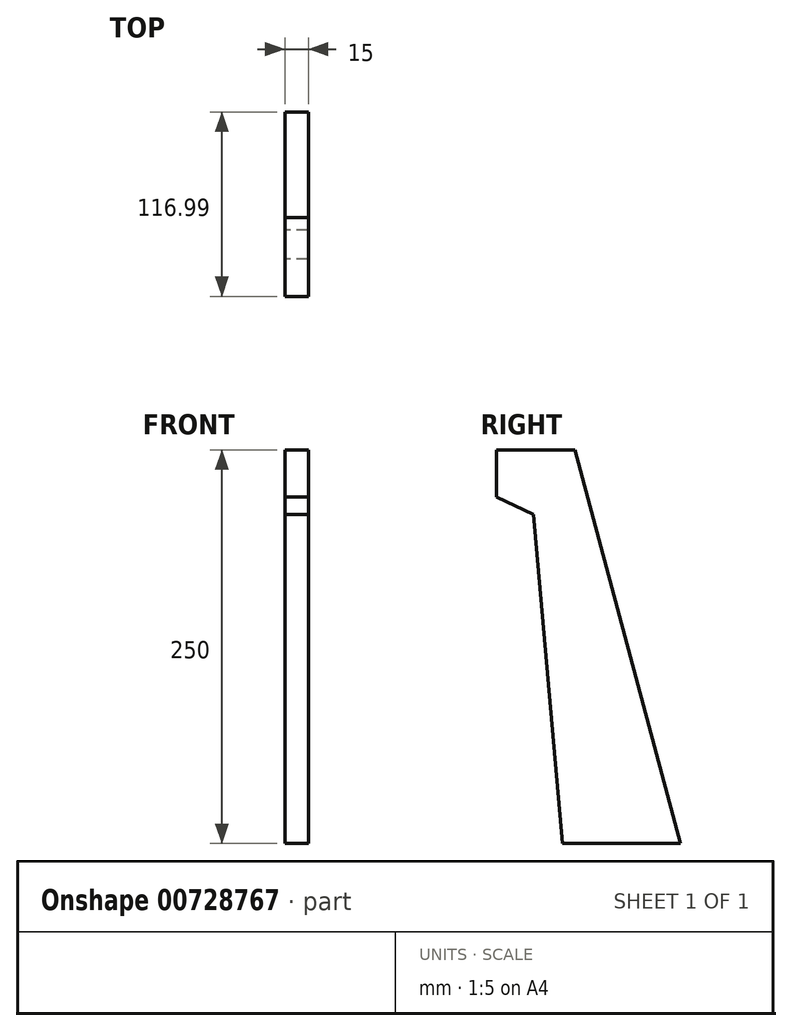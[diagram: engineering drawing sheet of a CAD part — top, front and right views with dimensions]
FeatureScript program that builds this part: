
annotation { "Feature Type Name" : "Feature", "Feature Type Description" : "" }
export const myFeature = defineFeature(function(context is Context, id is Id, definition is map)
    precondition{}
    {
        {
            var Q0;
            Q0=qCreatedBy(makeId("Right.planeOp"),FACE);
            var sketch = newSketch(context, id + "F0", { "sketchPlane" : qUnion([Q0])});
            skLineSegment(sketch, "E0", {"start": v(-75, 0) * mm, "end": v(75, 0) * mm, "construction": true});
            skLineSegment(sketch, "E1", {"start": v(75, 0) * mm, "end": v(8.01, 250) * mm});
            skLineSegment(sketch, "E2", {"start": v(8.01, 250) * mm, "end": v(-41.99, 250) * mm});
            skLineSegment(sketch, "E3", {"start": v(-75, 0) * mm, "end": v(54.9, 75) * mm});
            skSolve(sketch);
        }
        {
            var Q0;
            Q0=qCreatedBy(makeId("Right.planeOp"),FACE);
            var sketch = newSketch(context, id + "F1", { "sketchPlane" : qUnion([Q0])});
            skLineSegment(sketch, "E4.0", {"start": v(75, 0) * mm, "end": v(8.01, 250) * mm});
            skLineSegment(sketch, "E5.0", {"start": v(8.01, 250) * mm, "end": v(-41.99, 250) * mm});
            skLineSegment(sketch, "E6", {"start": v(-41.99, 250) * mm, "end": v(-41.99, 220) * mm});
            skLineSegment(sketch, "E7", {"start": v(-41.99, 220) * mm, "end": v(-18.28, 208.95) * mm});
            skLineSegment(sketch, "E8", {"start": v(-18.28, 208.95) * mm, "end": v(0, 0) * mm});
            skLineSegment(sketch, "E9", {"start": v(0, 0) * mm, "end": v(75, 0) * mm});
            skSolve(sketch);
        }
        {
            var Q0;
            Q0 = qSketchRegion(id + "F1", true);
            extrude(context, id + "F2", {"entities" : qUnion([Q0]), "endBound" : BoundingType.SYMMETRIC, "depth" : 15 * mm, "offsetDistance" : 25 * mm});
        }
        {
            var Q0;
            Q0=sQuery(id+"F0.wireOp",EDGE,"E3");
            cPlane(context, id + "F3", {"entities" : qUnion([Q0]), "cplaneType" : CPlaneType.LINE_ANGLE, "offset" : 25 * mm, "angle" : 0 * degree, "width" : 150 * mm, "height" : 150 * mm});
        }
    });
